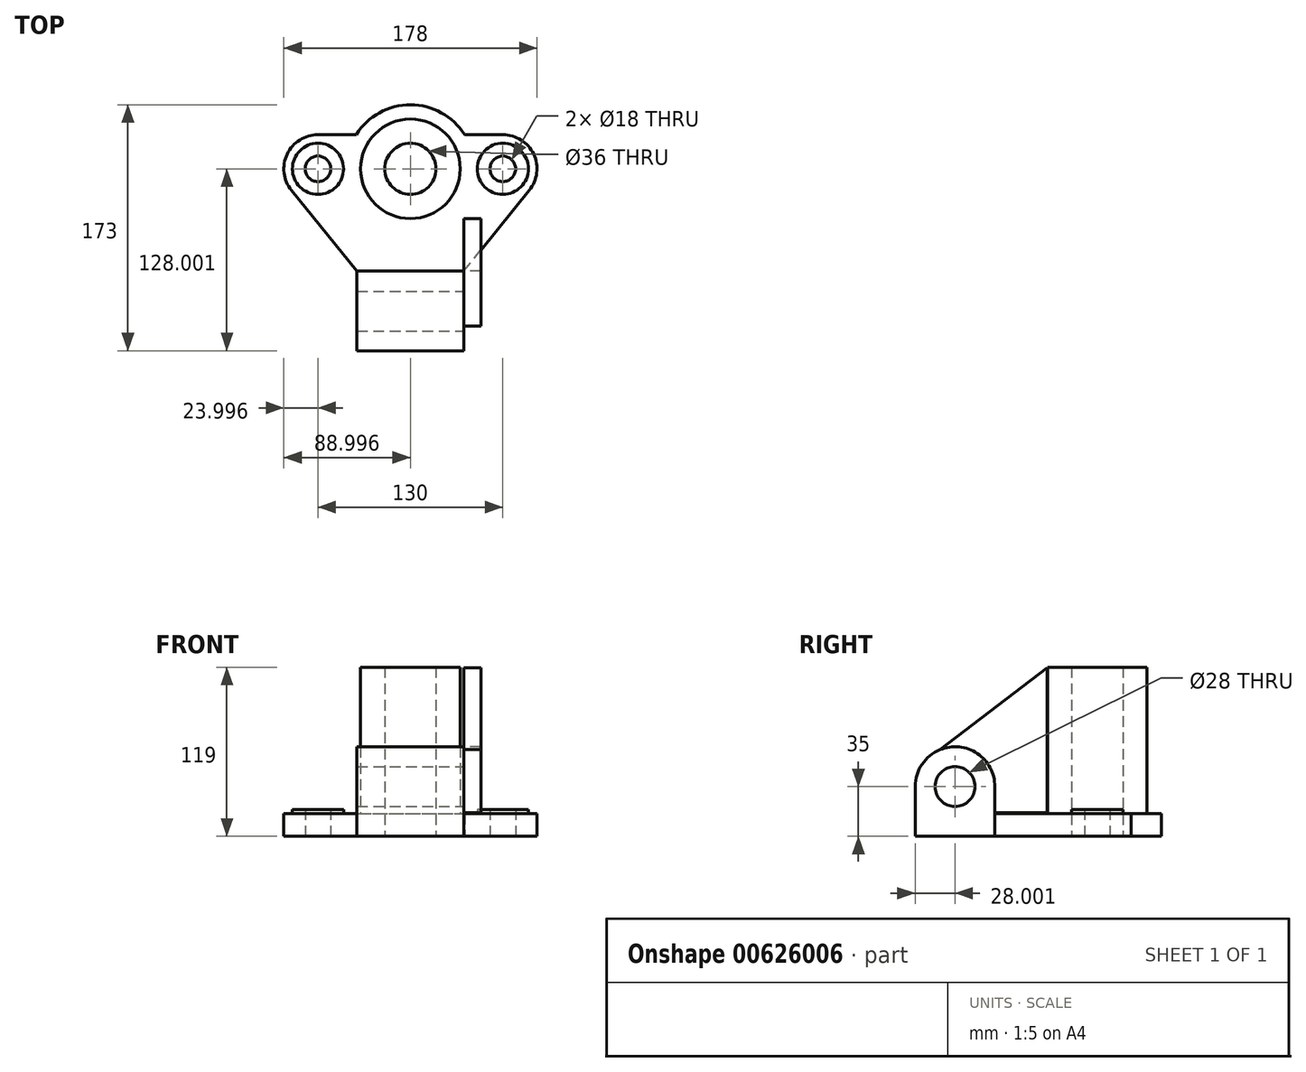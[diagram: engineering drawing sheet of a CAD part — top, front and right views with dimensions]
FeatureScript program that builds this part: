
annotation { "Feature Type Name" : "Feature", "Feature Type Description" : "" }
export const myFeature = defineFeature(function(context is Context, id is Id, definition is map)
    precondition{}
    {
        {
            var Q0;
            Q0=qCreatedBy(makeId("Top.planeOp"),FACE);
            var sketch = newSketch(context, id + "F0", { "sketchPlane" : qUnion([Q0])});
            skLineSegment(sketch, "E0.bottom", {"start": v(-33.04, -17.44) * mm, "end": v(41.96, -17.44) * mm});
            skLineSegment(sketch, "E0.top", {"start": v(-33.04, 38.56) * mm, "end": v(41.96, 38.56) * mm});
            skLineSegment(sketch, "E0.left", {"start": v(-33.04, -17.44) * mm, "end": v(-33.04, 38.56) * mm});
            skLineSegment(sketch, "E0.right", {"start": v(41.96, -17.44) * mm, "end": v(41.96, 38.56) * mm});
            skSolve(sketch);
        }
        {
            var Q0;
            Q0 = qSketchRegion(id + "F0", true);
            extrude(context, id + "F1", {"entities" : qUnion([Q0]), "depth" : 35 * mm, "offsetDistance" : 25 * mm});
        }
        {
            var Q0;
            Q0=makeQuery(id+"F1.opExtrude","CAP_FACE",FACE,{"disambiguationData":[OSD([sQuery(id+"F0.wireOp",EDGE,"E0.bottom"),sQuery(id+"F0.wireOp",EDGE,"E0.top"),sQuery(id+"F0.wireOp",EDGE,"E0.left"),sQuery(id+"F0.wireOp",EDGE,"E0.right")])],"isStart":true});
            var sketch = newSketch(context, id + "F2", { "sketchPlane" : qUnion([Q0])});
            skArc(sketch, "E1", {"start": v(-33.61, -134.56) * mm, "mid": v(4.46, -155.56) * mm, "end": v(42.52, -134.56) * mm});
            skPoint(sketch, "E1.centerSnap0", {"position": v(4.46, -38.56) * mm});
            skArc(sketch, "E2", {"start": v(-79.18, -95.44) * mm, "mid": v(-82.21, -120.88) * mm, "end": v(-60.54, -134.56) * mm});
            skArc(sketch, "E3", {"start": v(69.46, -134.56) * mm, "mid": v(91.12, -120.88) * mm, "end": v(88.1, -95.44) * mm});
            skLineSegment(sketch, "E4", {"start": v(41.96, -38.56) * mm, "end": v(88.1, -95.44) * mm});
            skLineSegment(sketch, "E5", {"start": v(69.46, -134.56) * mm, "end": v(42.52, -134.56) * mm});
            skLineSegment(sketch, "E6", {"start": v(-60.54, -134.56) * mm, "end": v(-33.61, -134.56) * mm});
            skLineSegment(sketch, "E7", {"start": v(-33.04, -38.56) * mm, "end": v(-79.18, -95.44) * mm});
            skSolve(sketch);
        }
        {
            var Q0;
            Q0=makeQuery(id+"F2.imprint","IMPRINT",FACE,{"disambiguationData":[TD([[makeQuery(id+"F2.imprint","IMPRINT",EDGE,{"derivedFrom":sQuery(id+"F2.wireOp",EDGE,"E1")}),1.0]])]});
            extrude(context, id + "F3", {"entities" : qUnion([Q0]), "oppositeDirection" : true, "depth" : 16 * mm, "offsetDistance" : 25 * mm});
        }
        {
            var Q0;
            Q0=makeQuery(id+"F3.opExtrude","CAP_FACE",FACE,{"disambiguationData":[OSD([sQuery(id+"F0.wireOp",EDGE,"E0.top"),sQuery(id+"F2.wireOp",EDGE,"E1"),sQuery(id+"F2.wireOp",EDGE,"E2"),sQuery(id+"F2.wireOp",EDGE,"E3"),sQuery(id+"F2.wireOp",EDGE,"E4"),sQuery(id+"F2.wireOp",EDGE,"E5"),sQuery(id+"F2.wireOp",EDGE,"E6"),sQuery(id+"F2.wireOp",EDGE,"E7")])],"isStart":false});
            var sketch = newSketch(context, id + "F4", { "sketchPlane" : qUnion([Q0])});
            skCircle(sketch, "E8", {"center": v(-60.54, 110.56) * mm, "radius": 18 * mm});
            skCircle(sketch, "E9", {"center": v(-60.54, 110.56) * mm, "radius": 9 * mm});
            skCircle(sketch, "E10", {"center": v(69.46, 110.56) * mm, "radius": 18 * mm});
            skCircle(sketch, "E11", {"center": v(69.46, 110.56) * mm, "radius": 9 * mm});
            skSolve(sketch);
        }
        {
            var Q0;
            Q0=makeQuery(id+"F4.imprint","IMPRINT",FACE,{"disambiguationData":[TD([[makeQuery(id+"F4.imprint","IMPRINT",EDGE,{"derivedFrom":sQuery(id+"F4.wireOp",EDGE,"E8")}),1.0]])]});
            var Q1;
            Q1=makeQuery(id+"F4.imprint","IMPRINT",FACE,{"disambiguationData":[TD([[makeQuery(id+"F4.imprint","IMPRINT",EDGE,{"derivedFrom":sQuery(id+"F4.wireOp",EDGE,"E10")}),1.0]])]});
            extrude(context, id + "F5", {"entities" : qUnion([Q0, Q1]), "operationType" : NewBodyOperationType.ADD, "depth" : 3 * mm, "offsetDistance" : 25 * mm});
        }
        {
            var Q0;
            Q0=makeQuery(id+"F5.boolean.opBoolean","SPLIT",FACE,{"disambiguationData":[TD([makeQuery(id+"F5.opExtrude","SWEPT_FACE",FACE,{"disambiguationData":[OSD([sQuery(id+"F4.wireOp",EDGE,"E9")])]})])],"derivedFrom":makeQuery(id+"F3.opExtrude","CAP_FACE",FACE,{"disambiguationData":[OSD([sQuery(id+"F0.wireOp",EDGE,"E0.top"),sQuery(id+"F2.wireOp",EDGE,"E1"),sQuery(id+"F2.wireOp",EDGE,"E2"),sQuery(id+"F2.wireOp",EDGE,"E3"),sQuery(id+"F2.wireOp",EDGE,"E4"),sQuery(id+"F2.wireOp",EDGE,"E5"),sQuery(id+"F2.wireOp",EDGE,"E6"),sQuery(id+"F2.wireOp",EDGE,"E7")])],"isStart":false})});
            var Q1;
            Q1=makeQuery(id+"F5.boolean.opBoolean","SPLIT",FACE,{"disambiguationData":[TD([makeQuery(id+"F5.opExtrude","SWEPT_FACE",FACE,{"disambiguationData":[OSD([sQuery(id+"F4.wireOp",EDGE,"E11")])]})])],"derivedFrom":makeQuery(id+"F3.opExtrude","CAP_FACE",FACE,{"disambiguationData":[OSD([sQuery(id+"F0.wireOp",EDGE,"E0.top"),sQuery(id+"F2.wireOp",EDGE,"E1"),sQuery(id+"F2.wireOp",EDGE,"E2"),sQuery(id+"F2.wireOp",EDGE,"E3"),sQuery(id+"F2.wireOp",EDGE,"E4"),sQuery(id+"F2.wireOp",EDGE,"E5"),sQuery(id+"F2.wireOp",EDGE,"E6"),sQuery(id+"F2.wireOp",EDGE,"E7")])],"isStart":false})});
            extrude(context, id + "F6", {"entities" : qUnion([Q0, Q1]), "operationType" : NewBodyOperationType.REMOVE, "endBound" : BoundingType.UP_TO_NEXT, "oppositeDirection" : true, "depth" : 25 * mm, "offsetDistance" : 25 * mm});
        }
        {
            var Q0;
            {var subQ0=sQuery(id+"F2.wireOp",EDGE,"E3");var subQ1=sQuery(id+"F2.wireOp",EDGE,"E2");var subQ2=sQuery(id+"F2.wireOp",EDGE,"E4");var subQ3=sQuery(id+"F2.wireOp",EDGE,"E1");var subQ4=sQuery(id+"F2.wireOp",EDGE,"E5");var subQ5=sQuery(id+"F2.wireOp",EDGE,"E6");var subQ6=sQuery(id+"F2.wireOp",EDGE,"E7");var subQ7=sQuery(id+"F0.wireOp",EDGE,"E0.top");Q0=makeQuery(id+"F5.boolean.opBoolean","SPLIT",FACE,{"disambiguationData":[TD([makeQuery(id+"F3.opExtrude","SWEPT_FACE",FACE,{"disambiguationData":[OSD([subQ3])]})])],"derivedFrom":makeQuery(id+"F3.opExtrude","CAP_FACE",FACE,{"disambiguationData":[OSD([subQ7,subQ3,subQ1,subQ0,subQ2,subQ4,subQ5,subQ6])],"isStart":false})});}
            var sketch = newSketch(context, id + "F7", { "sketchPlane" : qUnion([Q0])});
            skCircle(sketch, "E12", {"center": v(4.46, 110.56) * mm, "radius": 35 * mm});
            skCircle(sketch, "E13", {"center": v(4.46, 110.56) * mm, "radius": 18 * mm});
            skSolve(sketch);
        }
        {
            var Q0;
            Q0 = qSketchRegion(id + "F7", true);
            extrude(context, id + "F8", {"entities" : qUnion([Q0]), "operationType" : NewBodyOperationType.ADD, "depth" : 103 * mm, "offsetDistance" : 25 * mm});
        }
        {
            var Q0;
            {var subQ0=sQuery(id+"F2.wireOp",EDGE,"E3");var subQ1=sQuery(id+"F2.wireOp",EDGE,"E2");var subQ2=sQuery(id+"F2.wireOp",EDGE,"E4");var subQ3=sQuery(id+"F2.wireOp",EDGE,"E1");var subQ4=sQuery(id+"F2.wireOp",EDGE,"E5");var subQ5=sQuery(id+"F2.wireOp",EDGE,"E6");var subQ6=sQuery(id+"F2.wireOp",EDGE,"E7");var subQ7=sQuery(id+"F0.wireOp",EDGE,"E0.top");Q0=makeQuery(id+"F8.boolean.opBoolean","SPLIT",FACE,{"disambiguationData":[TD([makeQuery(id+"F8.opExtrude","SWEPT_FACE",FACE,{"disambiguationData":[OSD([sQuery(id+"F7.wireOp",EDGE,"E13")])]})])],"derivedFrom":makeQuery(id+"F5.boolean.opBoolean","SPLIT",FACE,{"disambiguationData":[TD([makeQuery(id+"F3.opExtrude","SWEPT_FACE",FACE,{"disambiguationData":[OSD([subQ3])]})])],"derivedFrom":makeQuery(id+"F3.opExtrude","CAP_FACE",FACE,{"disambiguationData":[OSD([subQ7,subQ3,subQ1,subQ0,subQ2,subQ4,subQ5,subQ6])],"isStart":false})})});}
            extrude(context, id + "F9", {"entities" : qUnion([Q0]), "operationType" : NewBodyOperationType.REMOVE, "endBound" : BoundingType.UP_TO_NEXT, "oppositeDirection" : true, "depth" : 25 * mm, "offsetDistance" : 25 * mm});
        }
        {
            var Q0;
            Q0=makeQuery(id+"F1.opExtrude","SWEPT_FACE",FACE,{"disambiguationData":[OSD([sQuery(id+"F0.wireOp",EDGE,"E0.right")])]});
            var sketch = newSketch(context, id + "F10", { "sketchPlane" : qUnion([Q0])});
            skLineSegment(sketch, "E14", {"start": v(-17.44, 35) * mm, "end": v(38.56, 35) * mm});
            skArc(sketch, "E15", {"start": v(38.56, 35) * mm, "mid": v(10.56, 63) * mm, "end": v(-17.44, 35) * mm});
            skSolve(sketch);
        }
        {
            var Q0;
            Q0 = qSketchRegion(id + "F10", true);
            extrude(context, id + "F11", {"entities" : qUnion([Q0]), "operationType" : NewBodyOperationType.ADD, "oppositeDirection" : true, "depth" : 75 * mm, "offsetDistance" : 25 * mm});
        }
        {
            var Q0;
            Q0=makeQuery(id+"F11.boolean.opBoolean","MERGE",FACE,{"derivedFrom":[makeQuery(id+"F1.opExtrude","SWEPT_FACE",FACE,{"disambiguationData":[OSD([sQuery(id+"F0.wireOp",EDGE,"E0.right")])]}),makeQuery(id+"F11.opExtrude","CAP_FACE",FACE,{"disambiguationData":[OSD([sQuery(id+"F10.wireOp",EDGE,"E14"),sQuery(id+"F10.wireOp",EDGE,"E15")])],"isStart":true})]});
            var sketch = newSketch(context, id + "F12", { "sketchPlane" : qUnion([Q0])});
            skCircle(sketch, "E16", {"center": v(10.56, 35) * mm, "radius": 14 * mm});
            skSolve(sketch);
        }
        {
            var Q0;
            Q0 = qSketchRegion(id + "F12", true);
            extrude(context, id + "F13", {"entities" : qUnion([Q0]), "operationType" : NewBodyOperationType.REMOVE, "endBound" : BoundingType.UP_TO_NEXT, "oppositeDirection" : true, "depth" : 25 * mm, "offsetDistance" : 25 * mm});
        }
        {
            var Q0;
            Q0=makeQuery(id+"F11.boolean.opBoolean","MERGE",FACE,{"derivedFrom":[makeQuery(id+"F1.opExtrude","SWEPT_FACE",FACE,{"disambiguationData":[OSD([sQuery(id+"F0.wireOp",EDGE,"E0.right")])]}),makeQuery(id+"F11.opExtrude","CAP_FACE",FACE,{"disambiguationData":[OSD([sQuery(id+"F10.wireOp",EDGE,"E14"),sQuery(id+"F10.wireOp",EDGE,"E15")])],"isStart":true})]});
            var sketch = newSketch(context, id + "F14", { "sketchPlane" : qUnion([Q0])});
            skLineSegment(sketch, "E17", {"start": v(0, 60.93) * mm, "end": v(75.51, 118.59) * mm});
            skLineSegment(sketch, "E18", {"start": v(75.51, 118.59) * mm, "end": v(75.51, 16.49) * mm});
            skLineSegment(sketch, "E19", {"start": v(75.51, 16.49) * mm, "end": v(38.56, 16.49) * mm});
            skPoint(sketch, "E19.endSnap0", {"position": v(38.56, 17.5) * mm});
            skLineSegment(sketch, "E20", {"start": v(38.56, 16.49) * mm, "end": v(38.56, 35) * mm});
            skArc(sketch, "E21", {"start": v(38.56, 35) * mm, "mid": v(26.19, 58.23) * mm, "end": v(0, 60.93) * mm});
            skSolve(sketch);
        }
        {
            var Q0;
            Q0=makeQuery(id+"F14.imprint","IMPRINT",FACE,{"disambiguationData":[TD([[makeQuery(id+"F14.imprint","IMPRINT",EDGE,{"derivedFrom":sQuery(id+"F14.wireOp",EDGE,"E17")}),-1.0]])]});
            extrude(context, id + "F15", {"entities" : qUnion([Q0]), "depth" : 12 * mm, "offsetDistance" : 25 * mm});
        }
    });
